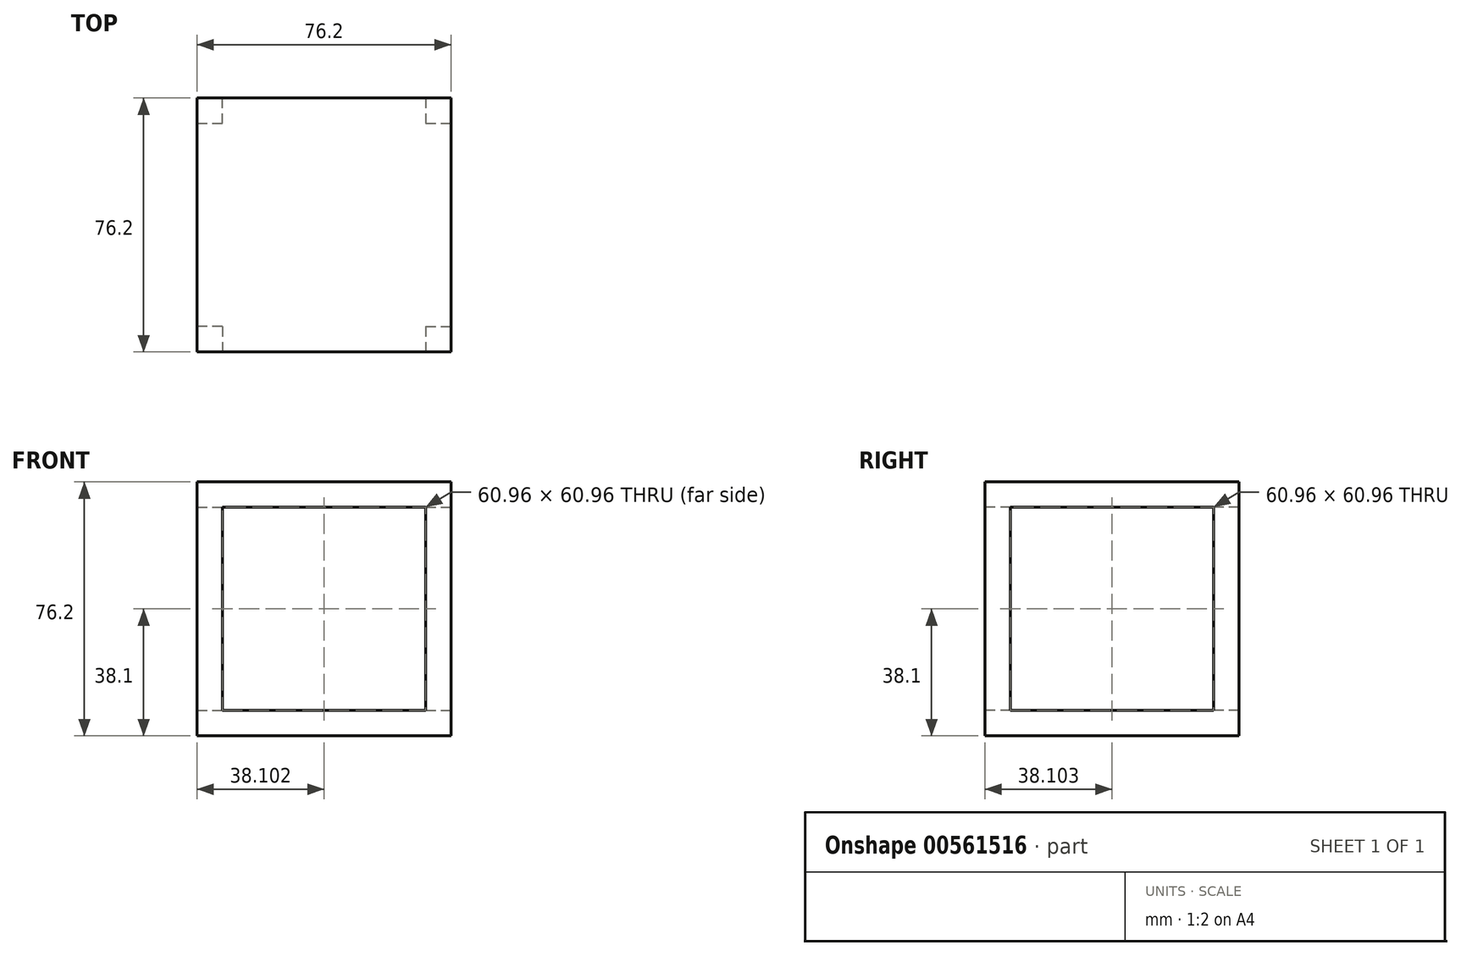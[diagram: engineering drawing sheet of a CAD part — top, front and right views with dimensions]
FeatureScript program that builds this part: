
annotation { "Feature Type Name" : "Feature", "Feature Type Description" : "" }
export const myFeature = defineFeature(function(context is Context, id is Id, definition is map)
    precondition{}
    {
        {
            var Q0;
            Q0=qCreatedBy(makeId("Top.planeOp"),FACE);
            var sketch = newSketch(context, id + "F0", { "sketchPlane" : qUnion([Q0])});
            skLineSegment(sketch, "E0.bottom", {"start": v(-41.72, 37.94) * mm, "end": v(34.48, 37.94) * mm});
            skLineSegment(sketch, "E0.top", {"start": v(-41.72, -38.26) * mm, "end": v(34.48, -38.26) * mm});
            skLineSegment(sketch, "E0.left", {"start": v(-41.72, 37.94) * mm, "end": v(-41.72, -38.26) * mm});
            skLineSegment(sketch, "E0.right", {"start": v(34.48, 37.94) * mm, "end": v(34.48, -38.26) * mm});
            skSolve(sketch);
        }
        {
            var Q0;
            Q0=makeQuery(id+"F0.imprint","IMPRINT",FACE,{"disambiguationData":[TD([[makeQuery(id+"F0.imprint","IMPRINT",EDGE,{"derivedFrom":sQuery(id+"F0.wireOp",EDGE,"E0.bottom")}),-1.0]])]});
            extrude(context, id + "F1", {"entities" : qUnion([Q0]), "depth" : 76.2 * mm, "offsetDistance" : 25.4 * mm});
        }
        {
            var Q0;
            Q0=makeQuery(id+"F1.opExtrude","SWEPT_FACE",FACE,{"disambiguationData":[OSD([sQuery(id+"F0.wireOp",EDGE,"E0.top")])]});
            shell(context, id + "F2", {"entities" : qUnion([Q0]), "thickness" : 7.62 * mm});
        }
        {
            var Q0;
            Q0=makeQuery(id+"F1.opExtrude","SWEPT_FACE",FACE,{"disambiguationData":[OSD([sQuery(id+"F0.wireOp",EDGE,"E0.left")])]});
            var sketch = newSketch(context, id + "F3", { "sketchPlane" : qUnion([Q0])});
            skLineSegment(sketch, "E1.bottom", {"start": v(-30.32, 68.58) * mm, "end": v(30.64, 68.58) * mm});
            skLineSegment(sketch, "E1.top", {"start": v(-30.32, 7.62) * mm, "end": v(30.64, 7.62) * mm});
            skLineSegment(sketch, "E1.left", {"start": v(-30.32, 68.58) * mm, "end": v(-30.32, 7.62) * mm});
            skLineSegment(sketch, "E1.right", {"start": v(30.64, 68.58) * mm, "end": v(30.64, 7.62) * mm});
            skSolve(sketch);
        }
        {
            var Q0;
            Q0=makeQuery(id+"F3.imprint","IMPRINT",FACE,{"disambiguationData":[TD([[makeQuery(id+"F3.imprint","IMPRINT",EDGE,{"derivedFrom":sQuery(id+"F3.wireOp",EDGE,"E1.bottom")}),-1.0]])]});
            extrude(context, id + "F4", {"entities" : qUnion([Q0]), "operationType" : NewBodyOperationType.REMOVE, "oppositeDirection" : true, "depth" : 25.4 * mm, "offsetDistance" : 25.4 * mm});
        }
        {
            var Q0;
            Q0=makeQuery(id+"F1.opExtrude","SWEPT_FACE",FACE,{"disambiguationData":[OSD([sQuery(id+"F0.wireOp",EDGE,"E0.bottom")])]});
            var sketch = newSketch(context, id + "F5", { "sketchPlane" : qUnion([Q0])});
            skLineSegment(sketch, "E2.bottom", {"start": v(34.1, 7.62) * mm, "end": v(-26.86, 7.62) * mm});
            skLineSegment(sketch, "E2.top", {"start": v(34.1, 68.58) * mm, "end": v(-26.86, 68.58) * mm});
            skLineSegment(sketch, "E2.left", {"start": v(34.1, 7.62) * mm, "end": v(34.1, 68.58) * mm});
            skLineSegment(sketch, "E2.right", {"start": v(-26.86, 7.62) * mm, "end": v(-26.86, 68.58) * mm});
            skSolve(sketch);
        }
        {
            var Q0;
            Q0=makeQuery(id+"F5.imprint","IMPRINT",FACE,{"disambiguationData":[TD([[makeQuery(id+"F5.imprint","IMPRINT",EDGE,{"derivedFrom":sQuery(id+"F5.wireOp",EDGE,"E2.bottom")}),-1.0]])]});
            extrude(context, id + "F6", {"entities" : qUnion([Q0]), "operationType" : NewBodyOperationType.REMOVE, "oppositeDirection" : true, "depth" : 25.4 * mm, "offsetDistance" : 25.4 * mm});
        }
        {
            var Q0;
            Q0=makeQuery(id+"F1.opExtrude","SWEPT_FACE",FACE,{"disambiguationData":[OSD([sQuery(id+"F0.wireOp",EDGE,"E0.right")])]});
            var sketch = newSketch(context, id + "F7", { "sketchPlane" : qUnion([Q0])});
            skLineSegment(sketch, "E3.bottom", {"start": v(-30.64, 68.58) * mm, "end": v(30.32, 68.58) * mm});
            skLineSegment(sketch, "E3.top", {"start": v(-30.64, 7.62) * mm, "end": v(30.32, 7.62) * mm});
            skLineSegment(sketch, "E3.left", {"start": v(-30.64, 68.58) * mm, "end": v(-30.64, 7.62) * mm});
            skLineSegment(sketch, "E3.right", {"start": v(30.32, 68.58) * mm, "end": v(30.32, 7.62) * mm});
            skSolve(sketch);
        }
        {
            var Q0;
            Q0=makeQuery(id+"F7.imprint","IMPRINT",FACE,{"disambiguationData":[TD([[makeQuery(id+"F7.imprint","IMPRINT",EDGE,{"derivedFrom":sQuery(id+"F7.wireOp",EDGE,"E3.bottom")}),-1.0]])]});
            extrude(context, id + "F8", {"entities" : qUnion([Q0]), "operationType" : NewBodyOperationType.REMOVE, "oppositeDirection" : true, "depth" : 25.4 * mm, "offsetDistance" : 25.4 * mm});
        }
    });
